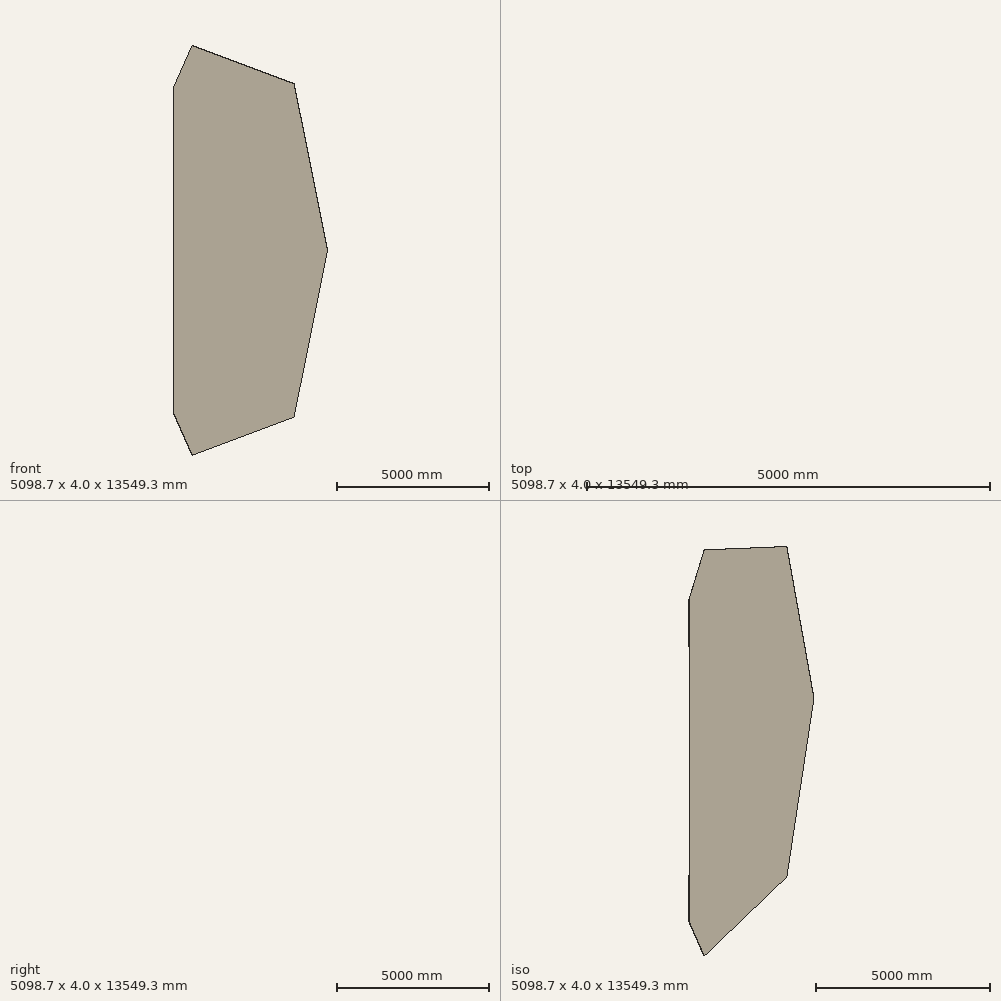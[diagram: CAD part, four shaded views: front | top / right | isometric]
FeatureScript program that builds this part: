
annotation { "Feature Type Name" : "Feature", "Feature Type Description" : "" }
export const myFeature = defineFeature(function(context is Context, id is Id, definition is map)
    precondition{}
    {
        {
            var Q0;
            Q0=qCreatedBy(makeId("Front.planeOp"),FACE);
            var sketch = newSketch(context, id + "F0", { "sketchPlane" : qUnion([Q0])});
            skLineSegment(sketch, "E0", {"start": v(-2549.33, 5368.4) * mm, "end": v(-1924.77, 6774.66) * mm});
            skLineSegment(sketch, "E1", {"start": v(-1924.77, 6774.66) * mm, "end": v(1440.1, 5513.65) * mm});
            skLineSegment(sketch, "E2", {"start": v(1440.1, 5513.65) * mm, "end": v(2549.33, 0) * mm});
            skLineSegment(sketch, "E3", {"start": v(2549.33, 0) * mm, "end": v(1440.1, -5513.63) * mm});
            skLineSegment(sketch, "E4", {"start": v(1440.1, -5513.63) * mm, "end": v(-1924.77, -6774.66) * mm});
            skLineSegment(sketch, "E5", {"start": v(-1924.77, -6774.66) * mm, "end": v(-2549.33, -5365.8) * mm});
            skLineSegment(sketch, "E6", {"start": v(-2549.33, -5365.8) * mm, "end": v(-2546.74, 0) * mm});
            skLineSegment(sketch, "E7", {"start": v(-2546.74, 0) * mm, "end": v(-2419.74, -0.05) * mm});
            skLineSegment(sketch, "E8", {"start": v(-2419.74, -0.05) * mm, "end": v(-2546.74, 0) * mm});
            skLineSegment(sketch, "E9", {"start": v(-2546.74, 0) * mm, "end": v(-2549.33, 5368.4) * mm});
            skSolve(sketch);
        }
        {
            var Q0;
            Q0 = qSketchRegion(id + "F0", true);
            extrude(context, id + "F1", {"entities" : qUnion([Q0]), "depth" : 4 * mm, "offsetDistance" : 25 * mm});
        }
    });
